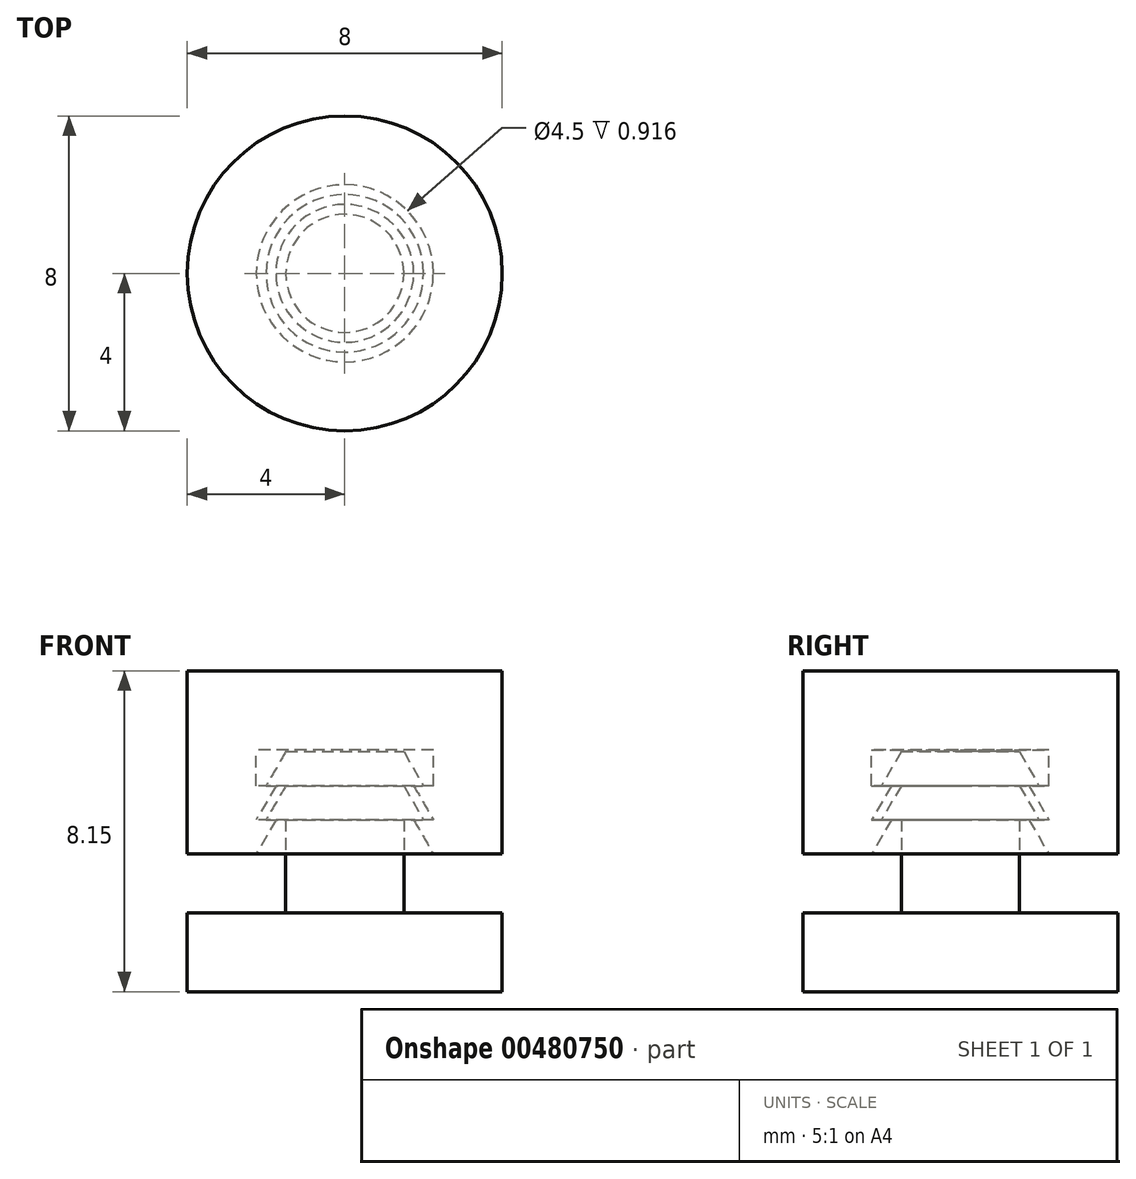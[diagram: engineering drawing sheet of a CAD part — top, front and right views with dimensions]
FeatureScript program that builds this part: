
annotation { "Feature Type Name" : "Feature", "Feature Type Description" : "" }
export const myFeature = defineFeature(function(context is Context, id is Id, definition is map)
    precondition{}
    {
        {
            var Q0;
            Q0=qCreatedBy(makeId("Front.planeOp"),FACE);
            var sketch = newSketch(context, id + "F0", { "sketchPlane" : qUnion([Q0])});
            skLineSegment(sketch, "E0.bottom", {"start": v(0, 0) * mm, "end": v(4, 0) * mm});
            skLineSegment(sketch, "E0.top", {"start": v(1.5, 2) * mm, "end": v(4, 2) * mm});
            skLineSegment(sketch, "E0.left", {"start": v(0, 0) * mm, "end": v(0, 2) * mm});
            skLineSegment(sketch, "E0.right", {"start": v(4, 0) * mm, "end": v(4, 2) * mm});
            skLineSegment(sketch, "E1.bottom", {"start": v(0, 0) * mm, "end": v(1.5, 0) * mm});
            skLineSegment(sketch, "E1.top", {"start": v(0, 6.1) * mm, "end": v(1.5, 6.1) * mm});
            skLineSegment(sketch, "E1.left", {"start": v(0, 0) * mm, "end": v(0, 6.1) * mm});
            skLineSegment(sketch, "E2", {"start": v(1.5, 6.1) * mm, "end": v(2, 5.23) * mm});
            skLineSegment(sketch, "E3", {"start": v(2, 5.23) * mm, "end": v(1.5, 5.23) * mm});
            skLineSegment(sketch, "E4", {"start": v(1.5, 5.23) * mm, "end": v(2, 4.37) * mm});
            skLineSegment(sketch, "E5", {"start": v(2, 4.37) * mm, "end": v(1.5, 4.37) * mm});
            skLineSegment(sketch, "E6", {"start": v(1.75, 5.23) * mm, "end": v(2.25, 4.37) * mm});
            skLineSegment(sketch, "E7", {"start": v(1.75, 5.23) * mm, "end": v(2.25, 5.23) * mm});
            skLineSegment(sketch, "E8", {"start": v(2, 4.37) * mm, "end": v(2.25, 4.37) * mm});
            skLineSegment(sketch, "E9", {"start": v(1.75, 4.37) * mm, "end": v(2.25, 3.5) * mm});
            skLineSegment(sketch, "E10", {"start": v(2.25, 3.5) * mm, "end": v(4, 3.5) * mm});
            skLineSegment(sketch, "E11", {"start": v(0, 6.15) * mm, "end": v(2.25, 6.15) * mm});
            skLineSegment(sketch, "E12", {"start": v(2.25, 6.15) * mm, "end": v(2.25, 5.23) * mm});
            skLineSegment(sketch, "E13", {"start": v(0, 8.15) * mm, "end": v(4, 8.15) * mm});
            skLineSegment(sketch, "E14", {"start": v(0, 8.15) * mm, "end": v(0, 6.15) * mm});
            skLineSegment(sketch, "E15", {"start": v(4, 8.15) * mm, "end": v(4, 3.5) * mm});
            skLineSegment(sketch, "E16", {"start": v(1.5, 6.1) * mm, "end": v(1.5, 2) * mm});
            skSolve(sketch);
        }
        {
            var Q0;
            Q0=makeQuery(id+"F0.imprint","IMPRINT",FACE,{"disambiguationData":[TD([[makeQuery(id+"F0.imprint","IMPRINT",EDGE,{"derivedFrom":sQuery(id+"F0.wireOp",EDGE,"E0.bottom")}),1.0]])]});
            var Q1;
            {var subQ0=sQuery(id+"F0.wireOp",EDGE,"E2");Q1=makeQuery(id+"F0.imprint","IMPRINT",FACE,{"disambiguationData":[TD([[makeQuery(id+"F0.imprint","IMPRINT",EDGE,{"derivedFrom":subQ0}),-1.0]])]});}
            var Q2;
            {var subQ0=sQuery(id+"F0.wireOp",EDGE,"E4");Q2=makeQuery(id+"F0.imprint","IMPRINT",FACE,{"disambiguationData":[TD([[makeQuery(id+"F0.imprint","IMPRINT",EDGE,{"derivedFrom":subQ0}),-1.0]])]});}
            var Q3;
            Q3=sQuery(id+"F0.wireOp",EDGE,"E1.left");
            revolve(context, id + "F1", {"entities" : qUnion([Q0, Q1, Q2]), "axis" : qUnion([Q3]), "revolveType" : RevolveType.FULL});
        }
        {
            var Q0;
            {var subQ4=sQuery(id+"F0.wireOp",EDGE,"E6");Q0=makeQuery(id+"F0.imprint","IMPRINT",FACE,{"disambiguationData":[TD([[makeQuery(id+"F0.imprint","IMPRINT",EDGE,{"derivedFrom":subQ4}),1.0]])]});}
            var Q1;
            Q1=sQuery(id+"F0.wireOp",EDGE,"E14");
            revolve(context, id + "F2", {"entities" : qUnion([Q0]), "axis" : qUnion([Q1]), "revolveType" : RevolveType.FULL});
        }
    });
